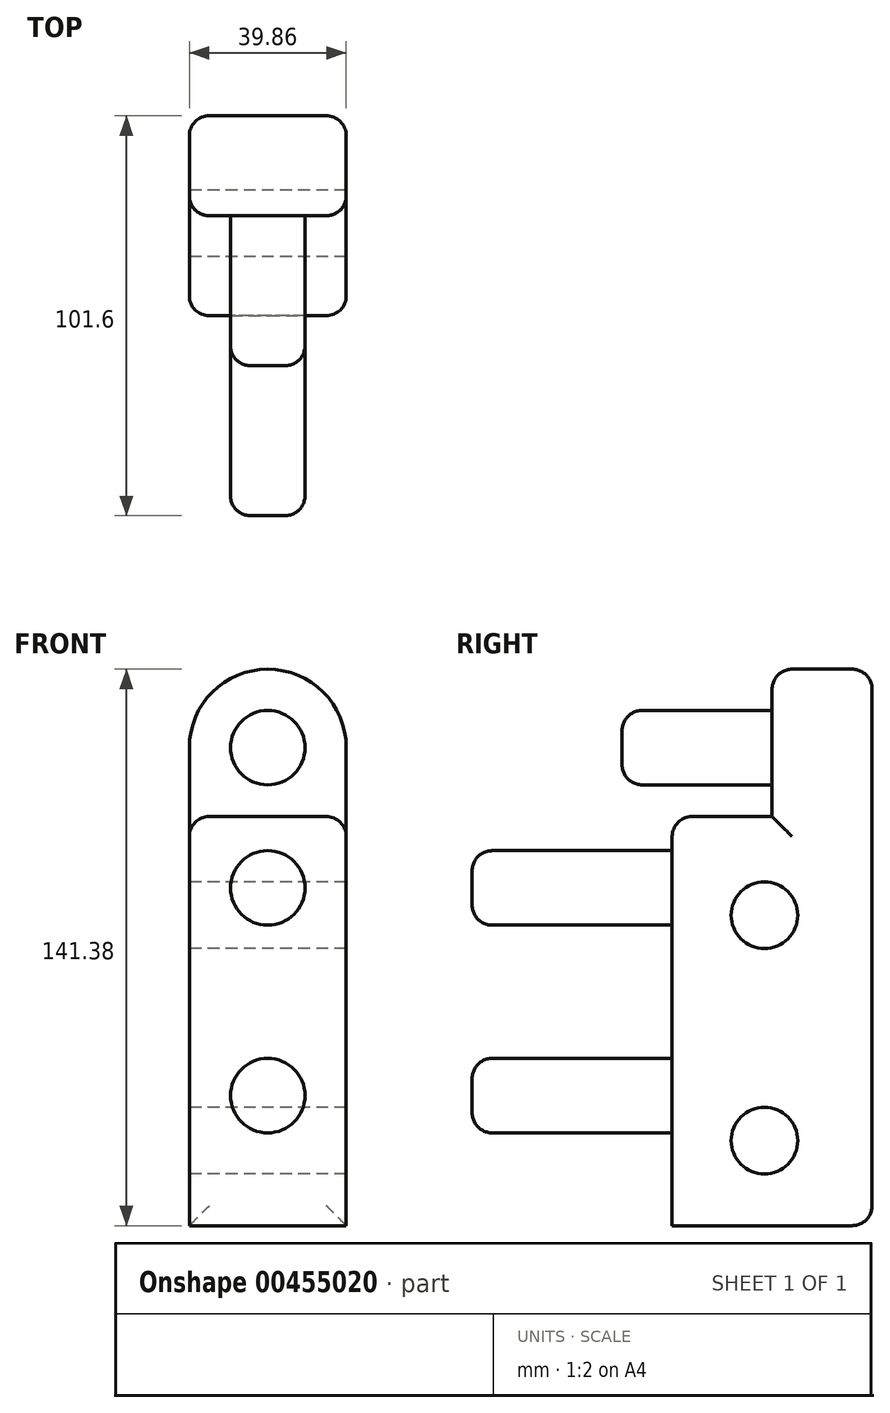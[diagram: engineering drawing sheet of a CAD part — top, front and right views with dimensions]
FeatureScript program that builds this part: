
annotation { "Feature Type Name" : "Feature", "Feature Type Description" : "" }
export const myFeature = defineFeature(function(context is Context, id is Id, definition is map)
    precondition{}
    {
        {
            var Q0;
            Q0=qCreatedBy(makeId("Front.planeOp"),FACE);
            var sketch = newSketch(context, id + "F0", { "sketchPlane" : qUnion([Q0])});
            skArc(sketch, "E0", {"start": v(19.93, 0) * mm, "mid": v(0, 19.93) * mm, "end": v(-19.93, 0) * mm});
            skLineSegment(sketch, "E1", {"start": v(-19.93, 0) * mm, "end": v(-19.93, -121.45) * mm});
            skLineSegment(sketch, "E2", {"start": v(19.93, 0) * mm, "end": v(19.93, -121.45) * mm});
            skArc(sketch, "E3", {"start": v(19.93, -121.45) * mm, "mid": v(0, -141.38) * mm, "end": v(-19.93, -121.45) * mm});
            skLineSegment(sketch, "E4", {"start": v(19.93, -121.45) * mm, "end": v(-19.93, -121.45) * mm});
            skLineSegment(sketch, "E5", {"start": v(19.93, -17.52) * mm, "end": v(-19.93, -17.52) * mm});
            skCircle(sketch, "E6", {"center": v(0, 0) * mm, "radius": 9.46 * mm});
            skCircle(sketch, "E7", {"center": v(0, -35.64) * mm, "radius": 9.46 * mm});
            skPoint(sketch, "E7.centerSnap0", {"position": v(0, -17.52) * mm});
            skCircle(sketch, "E8", {"center": v(0, -88.4) * mm, "radius": 9.46 * mm});
            skSolve(sketch);
        }
        {
            var Q0;
            Q0=makeQuery(id+"F0.imprint","IMPRINT",FACE,{"disambiguationData":[TD([[makeQuery(id+"F0.imprint","IMPRINT",EDGE,{"derivedFrom":sQuery(id+"F0.wireOp",EDGE,"E7")}),1.0]])]});
            var Q1;
            Q1=makeQuery(id+"F0.imprint","IMPRINT",FACE,{"disambiguationData":[TD([[makeQuery(id+"F0.imprint","IMPRINT",EDGE,{"derivedFrom":sQuery(id+"F0.wireOp",EDGE,"E8")}),1.0]])]});
            extrude(context, id + "F1", {"entities" : qUnion([Q0, Q1]), "depth" : 101.6 * mm, "offsetDistance" : 25.4 * mm});
        }
        {
            var Q0;
            {var subQ0=sQuery(id+"F0.wireOp",EDGE,"E4");Q0=makeQuery(id+"F0.imprint","IMPRINT",FACE,{"disambiguationData":[TD([[makeQuery(id+"F0.imprint","IMPRINT",EDGE,{"derivedFrom":subQ0}),-1.0]])]});}
            var Q1;
            Q1=makeQuery(id+"F0.imprint","IMPRINT",FACE,{"disambiguationData":[TD([[makeQuery(id+"F0.imprint","IMPRINT",EDGE,{"derivedFrom":sQuery(id+"F0.wireOp",EDGE,"E3")}),-1.0]])]});
            extrude(context, id + "F2", {"entities" : qUnion([Q0, Q1]), "operationType" : NewBodyOperationType.ADD, "depth" : 50.8 * mm, "offsetDistance" : 25.4 * mm});
        }
        {
            var Q0;
            {var subQ2=sQuery(id+"F0.wireOp",EDGE,"E0");Q0=makeQuery(id+"F0.imprint","IMPRINT",FACE,{"disambiguationData":[TD([[makeQuery(id+"F0.imprint","IMPRINT",EDGE,{"derivedFrom":subQ2}),1.0]])]});}
            extrude(context, id + "F3", {"entities" : qUnion([Q0]), "operationType" : NewBodyOperationType.ADD, "depth" : 25.4 * mm, "offsetDistance" : 25.4 * mm});
        }
        {
            var Q0;
            Q0=makeQuery(id+"F0.imprint","IMPRINT",FACE,{"disambiguationData":[TD([[makeQuery(id+"F0.imprint","IMPRINT",EDGE,{"derivedFrom":sQuery(id+"F0.wireOp",EDGE,"E6")}),1.0]])]});
            extrude(context, id + "F4", {"entities" : qUnion([Q0]), "operationType" : NewBodyOperationType.ADD, "depth" : 63.5 * mm, "offsetDistance" : 25.4 * mm});
        }
        {
            var Q0;
            Q0=makeQuery(id+"F2.opExtrude","CAP_EDGE",EDGE,{"disambiguationData":[OSD([sQuery(id+"F0.wireOp",EDGE,"E1")])],"isStart":false});
            var Q1;
            Q1=makeQuery(id+"F2.opExtrude","SWEPT_EDGE",EDGE,{"disambiguationData":[OSD([sQuery(id+"F0.wireOp",EDGE,"E1"),sQuery(id+"F0.wireOp",EDGE,"E5")])]});
            var Q2;
            Q2=makeQuery(id+"F2.opExtrude","CAP_EDGE",EDGE,{"disambiguationData":[OSD([sQuery(id+"F0.wireOp",EDGE,"E2")])],"isStart":false});
            var Q3;
            Q3=makeQuery(id+"F2.opExtrude","CAP_EDGE",EDGE,{"disambiguationData":[OSD([sQuery(id+"F0.wireOp",EDGE,"E5")])],"isStart":false});
            var Q4;
            Q4=makeQuery(id+"F2.opExtrude","SWEPT_EDGE",EDGE,{"disambiguationData":[OSD([sQuery(id+"F0.wireOp",EDGE,"E2"),sQuery(id+"F0.wireOp",EDGE,"E5")])]});
            fillet(context, id + "F5", {"entities" : qUnion([Q0, Q1, Q2, Q3, Q4]), "radius" : 5.08 * mm, "tangentPropagation" : true, "allowEdgeOverflow" : false});
        }
        {
            var Q0;
            {var subQ0=sQuery(id+"F0.wireOp",EDGE,"E6");var subQ1=sQuery(id+"F0.wireOp",EDGE,"E5");var subQ2=sQuery(id+"F0.wireOp",EDGE,"E2");var subQ3=sQuery(id+"F0.wireOp",EDGE,"E1");var subQ4=sQuery(id+"F0.wireOp",EDGE,"E8");var subQ5=sQuery(id+"F0.wireOp",EDGE,"E7");Q0=makeQuery(id+"F4.boolean.opBoolean","MERGE",FACE,{"derivedFrom":[makeQuery(id+"F3.boolean.opBoolean","MERGE",FACE,{"derivedFrom":[makeQuery(id+"F2.boolean.opBoolean","MERGE",FACE,{"derivedFrom":[makeQuery(id+"F1.opExtrude","CAP_FACE",FACE,{"disambiguationData":[OSD([subQ5])],"isStart":true}),makeQuery(id+"F1.opExtrude","CAP_FACE",FACE,{"disambiguationData":[OSD([subQ4])],"isStart":true}),makeQuery(id+"F2.opExtrude","CAP_FACE",FACE,{"disambiguationData":[OSD([subQ3,subQ2,sQuery(id+"F0.wireOp",EDGE,"E3"),subQ1,subQ5,subQ4])],"isStart":true})]}),makeQuery(id+"F3.opExtrude","CAP_FACE",FACE,{"disambiguationData":[OSD([sQuery(id+"F0.wireOp",EDGE,"E0"),subQ3,subQ2,subQ1,subQ0])],"isStart":true})]}),makeQuery(id+"F4.opExtrude","CAP_FACE",FACE,{"disambiguationData":[OSD([subQ0])],"isStart":true})]});}
            fillet(context, id + "F6", {"entities" : qUnion([Q0]), "radius" : 5.08 * mm, "tangentPropagation" : true, "allowEdgeOverflow" : false});
        }
        {
            var Q0;
            Q0=makeQuery(id+"F3.opExtrude","CAP_EDGE",EDGE,{"disambiguationData":[OSD([sQuery(id+"F0.wireOp",EDGE,"E1")])],"isStart":false});
            var Q1;
            Q1=makeQuery(id+"F3.opExtrude","CAP_EDGE",EDGE,{"disambiguationData":[OSD([sQuery(id+"F0.wireOp",EDGE,"E0")])],"isStart":false});
            var Q2;
            Q2=makeQuery(id+"F3.opExtrude","SWEPT_EDGE",EDGE,{"disambiguationData":[OSD([sQuery(id+"F0.wireOp",EDGE,"E0"),sQuery(id+"F0.wireOp",EDGE,"E2")])]});
            fillet(context, id + "F7", {"entities" : qUnion([Q0, Q1, Q2]), "radius" : 5.08 * mm, "tangentPropagation" : true, "allowEdgeOverflow" : false});
        }
        {
            var Q0;
            Q0=qCreatedBy(makeId("Right.planeOp"),FACE);
            var sketch = newSketch(context, id + "F8", { "sketchPlane" : qUnion([Q0])});
            skCircle(sketch, "E9", {"center": v(-27.35, -42.58) * mm, "radius": 8.46 * mm});
            skCircle(sketch, "E10", {"center": v(-27.35, -99.84) * mm, "radius": 8.46 * mm});
            skSolve(sketch);
        }
        {
            var Q0;
            Q0 = qSketchRegion(id + "F8", true);
            extrude(context, id + "F9", {"entities" : qUnion([Q0]), "operationType" : NewBodyOperationType.REMOVE, "endBound" : BoundingType.SYMMETRIC, "depth" : 50.8 * mm, "offsetDistance" : 25.4 * mm});
        }
        {
            var Q0;
            Q0=qCreatedBy(makeId("Right.planeOp"),FACE);
            var sketch = newSketch(context, id + "F10", { "sketchPlane" : qUnion([Q0])});
            skCircle(sketch, "E11.0", {"center": v(-27.35, -42.58) * mm, "radius": 4.74 * mm});
            skCircle(sketch, "E12.0", {"center": v(-27.35, -42.58) * mm, "radius": 8.46 * mm});
            skCircle(sketch, "E13.0", {"center": v(-27.35, -99.84) * mm, "radius": 8.46 * mm});
            skCircle(sketch, "E14", {"center": v(-27.35, -99.84) * mm, "radius": 4.74 * mm});
            skSolve(sketch);
        }
        {
            var Q0;
            Q0=sQuery(id+"F10.wireOp",EDGE,"E11.0");
            var Q1;
            Q1=sQuery(id+"F10.wireOp",EDGE,"E14");
            extrude(context, id + "F11", {"bodyType" : ToolBodyType.SURFACE, "surfaceEntities" : qUnion([Q0, Q1]), "endBound" : BoundingType.SYMMETRIC, "depth" : 50.8 * mm, "offsetDistance" : 25.4 * mm});
        }
        {
            var Q0;
            Q0=makeQuery(id+"F1.opExtrude","CAP_EDGE",EDGE,{"disambiguationData":[OSD([sQuery(id+"F0.wireOp",EDGE,"E8")])],"isStart":false});
            var Q1;
            Q1=makeQuery(id+"F1.opExtrude","CAP_EDGE",EDGE,{"disambiguationData":[OSD([sQuery(id+"F0.wireOp",EDGE,"E7")])],"isStart":false});
            var Q2;
            Q2=makeQuery(id+"F4.opExtrude","CAP_EDGE",EDGE,{"disambiguationData":[OSD([sQuery(id+"F0.wireOp",EDGE,"E6")])],"isStart":false});
            fillet(context, id + "F12", {"entities" : qUnion([Q0, Q1, Q2]), "radius" : 5.08 * mm, "tangentPropagation" : true, "allowEdgeOverflow" : false});
        }
    });
